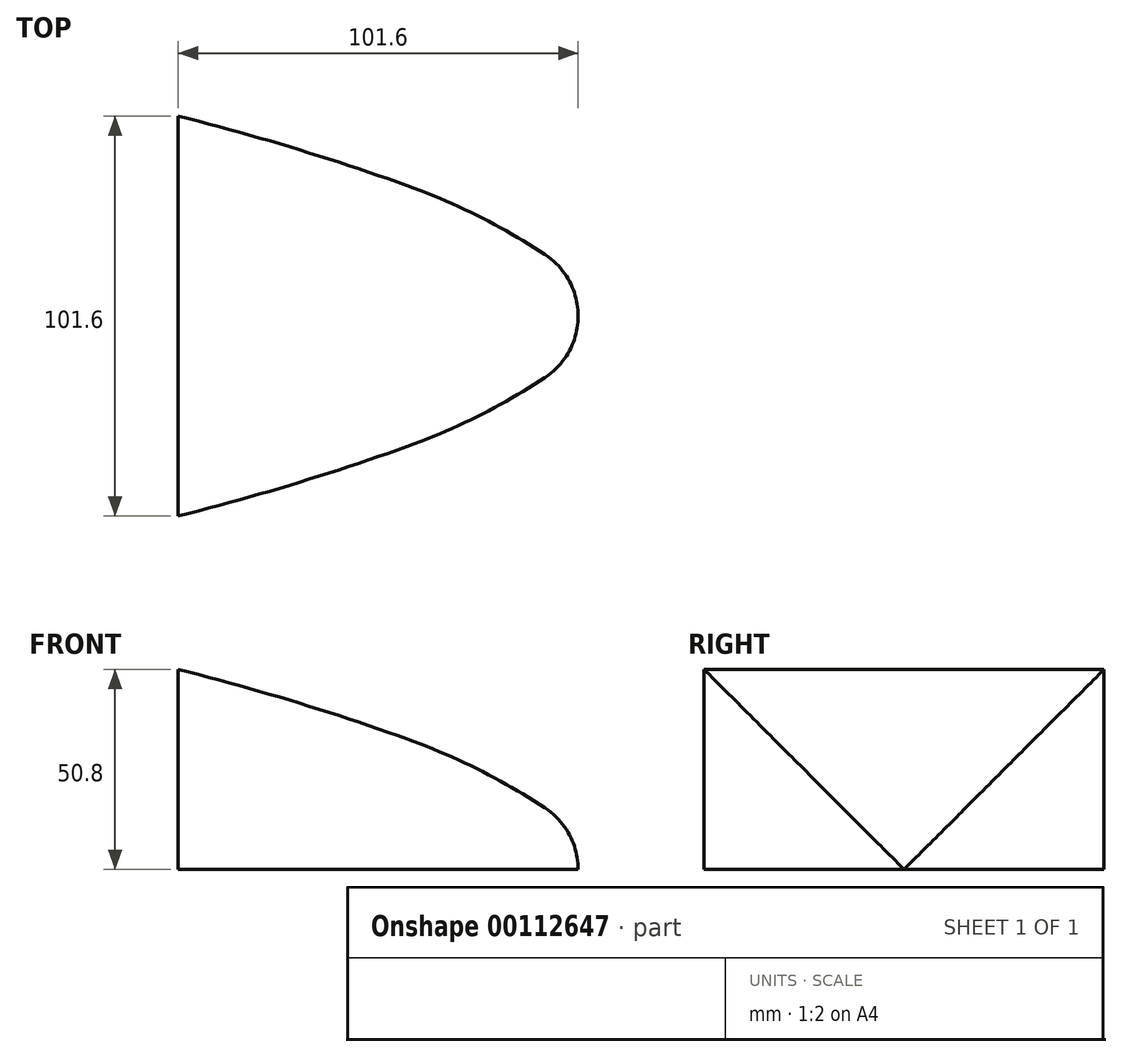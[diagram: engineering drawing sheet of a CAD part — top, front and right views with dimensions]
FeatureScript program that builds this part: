
annotation { "Feature Type Name" : "Feature", "Feature Type Description" : "" }
export const myFeature = defineFeature(function(context is Context, id is Id, definition is map)
    precondition{}
    {
        {
            var Q0;
            Q0=qCreatedBy(makeId("Top.planeOp"),FACE);
            var sketch = newSketch(context, id + "F0", { "sketchPlane" : qUnion([Q0])});
            skLineSegment(sketch, "E0", {"start": v(0, 0) * mm, "end": v(-25.4, 0) * mm, "construction": true});
            skLineSegment(sketch, "E1", {"start": v(0, 0) * mm, "end": v(0, -25.4) * mm, "construction": true});
            skLineSegment(sketch, "E2", {"start": v(0, -25.4) * mm, "end": v(-25.4, -25.4) * mm, "construction": true});
            skLineSegment(sketch, "E3", {"start": v(-25.4, 0) * mm, "end": v(-25.4, -25.4) * mm, "construction": true});
            skArc(sketch, "E4", {"start": v(-8.41, -15.61) * mm, "mid": v(-2.24, -8.87) * mm, "end": v(0, 0) * mm});
            skLineSegment(sketch, "E5", {"start": v(0, 0) * mm, "end": v(-25.4, -25.4) * mm, "construction": true});
            skLineSegment(sketch, "E6", {"start": v(-25.4, -25.4) * mm, "end": v(-50.8, -25.4) * mm, "construction": true});
            skLineSegment(sketch, "E7", {"start": v(-50.8, -25.4) * mm, "end": v(-76.2, -25.4) * mm, "construction": true});
            skLineSegment(sketch, "E8", {"start": v(-76.2, -25.4) * mm, "end": v(-76.2, -50.8) * mm, "construction": true});
            skLineSegment(sketch, "E9", {"start": v(-25.4, -25.4) * mm, "end": v(-76.2, -50.8) * mm, "construction": true});
            skLineSegment(sketch, "E10", {"start": v(0, -25.4) * mm, "end": v(0, -50.8) * mm, "construction": true});
            skLineSegment(sketch, "E11", {"start": v(0, -50.8) * mm, "end": v(-25.4, -50.8) * mm, "construction": true});
            skLineSegment(sketch, "E12", {"start": v(-25.4, -25.4) * mm, "end": v(-25.4, -50.8) * mm, "construction": true});
            skLineSegment(sketch, "E13", {"start": v(-76.2, -25.4) * mm, "end": v(-101.6, -25.4) * mm, "construction": true});
            skLineSegment(sketch, "E14", {"start": v(-101.6, -25.4) * mm, "end": v(-101.6, -50.8) * mm, "construction": true});
            skLineSegment(sketch, "E15", {"start": v(-76.2, -50.8) * mm, "end": v(-50.8, -50.8) * mm, "construction": true});
            skLineSegment(sketch, "E16", {"start": v(-50.8, -50.8) * mm, "end": v(-25.4, -50.8) * mm, "construction": true});
            skLineSegment(sketch, "E17", {"start": v(-76.2, -50.8) * mm, "end": v(-101.6, -50.8) * mm, "construction": true});
            skLineSegment(sketch, "E18", {"start": v(-101.6, -50.8) * mm, "end": v(-127, -50.8) * mm, "construction": true});
            skLineSegment(sketch, "E19", {"start": v(-127, -50.8) * mm, "end": v(-152.4, -50.8) * mm, "construction": true});
            skLineSegment(sketch, "E20", {"start": v(-152.4, -50.8) * mm, "end": v(-177.8, -50.8) * mm, "construction": true});
            skLineSegment(sketch, "E21", {"start": v(-177.8, -50.8) * mm, "end": v(-203.2, -50.8) * mm, "construction": true});
            skLineSegment(sketch, "E22", {"start": v(-203.2, -50.8) * mm, "end": v(-203.2, -76.2) * mm, "construction": true});
            skLineSegment(sketch, "E23", {"start": v(-101.6, -50.8) * mm, "end": v(-203.2, -76.2) * mm, "construction": true});
            skArc(sketch, "E24", {"start": v(-101.6, -50.8) * mm, "mid": v(-72.29, -42.69) * mm, "end": v(-43.42, -33.11) * mm});
            skArc(sketch, "E25", {"start": v(-43.42, -33.11) * mm, "mid": v(-25.4, -25.4) * mm, "end": v(-8.41, -15.61) * mm});
            skLineSegment(sketch, "E26", {"start": v(0, 0) * mm, "end": v(-101.6, 0) * mm});
            skLineSegment(sketch, "E27", {"start": v(-101.6, -50.8) * mm, "end": v(-101.6, 0) * mm});
            skArc(sketch, "E28", {"start": v(0, 0) * mm, "mid": v(-2.24, 8.87) * mm, "end": v(-8.41, 15.61) * mm});
            skArc(sketch, "E29", {"start": v(-8.41, 15.61) * mm, "mid": v(-25.4, 25.4) * mm, "end": v(-43.42, 33.11) * mm});
            skLineSegment(sketch, "E30", {"start": v(-25.4, 0) * mm, "end": v(-25.4, 25.4) * mm, "construction": true});
            skArc(sketch, "E31", {"start": v(-43.42, 33.11) * mm, "mid": v(-72.29, 42.69) * mm, "end": v(-101.6, 50.8) * mm});
            skLineSegment(sketch, "E32", {"start": v(-101.6, 0) * mm, "end": v(-101.6, 50.8) * mm});
            skSolve(sketch);
        }
        {
            var Q0;
            Q0=makeQuery(id+"F0.imprint","IMPRINT",FACE,{"disambiguationData":[TD([[makeQuery(id+"F0.imprint","IMPRINT",EDGE,{"derivedFrom":sQuery(id+"F0.wireOp",EDGE,"E4")}),1.0]])]});
            var Q1;
            Q1=makeQuery(id+"F0.imprint","IMPRINT",FACE,{"disambiguationData":[TD([[makeQuery(id+"F0.imprint","IMPRINT",EDGE,{"derivedFrom":sQuery(id+"F0.wireOp",EDGE,"E26")}),-1.0]])]});
            extrude(context, id + "F1", {"entities" : qUnion([Q0, Q1]), "depth" : 101.6 * mm});
        }
        {
            var Q0;
            Q0=qCreatedBy(makeId("Front.planeOp"),FACE);
            var sketch = newSketch(context, id + "F2", { "sketchPlane" : qUnion([Q0])});
            skArc(sketch, "E33", {"start": v(0, 0) * mm, "mid": v(-2.24, 8.87) * mm, "end": v(-8.41, 15.61) * mm});
            skLineSegment(sketch, "E34.bottom", {"start": v(0, 0) * mm, "end": v(-101.6, 0) * mm, "construction": true});
            skLineSegment(sketch, "E34.top", {"start": v(0, 464.33) * mm, "end": v(-101.6, 464.33) * mm});
            skLineSegment(sketch, "E34.left", {"start": v(0, 0) * mm, "end": v(0, 464.33) * mm});
            skLineSegment(sketch, "E34.right", {"start": v(-101.6, 0) * mm, "end": v(-101.6, 464.33) * mm});
            skArc(sketch, "E35", {"start": v(-8.41, 15.61) * mm, "mid": v(-25.4, 25.4) * mm, "end": v(-43.42, 33.11) * mm});
            skArc(sketch, "E36", {"start": v(-43.42, 33.11) * mm, "mid": v(-72.29, 42.69) * mm, "end": v(-101.6, 50.8) * mm});
            skLineSegment(sketch, "E37", {"start": v(-101.6, 50.8) * mm, "end": v(-203.2, 50.8) * mm, "construction": true});
            skLineSegment(sketch, "E38", {"start": v(-203.2, 50.8) * mm, "end": v(-203.2, 76.2) * mm, "construction": true});
            skLineSegment(sketch, "E39", {"start": v(-203.2, 76.2) * mm, "end": v(-101.6, 50.8) * mm, "construction": true});
            skSolve(sketch);
        }
        {
            var Q0;
            Q0 = qSketchRegion(id + "F2", true);
            var Q1;
            Q1=makeQuery(id+"F1.opExtrude","SWEPT_FACE",FACE,{"disambiguationData":[OSD([sQuery(id+"F0.wireOp",EDGE,"E24")])]});
            var Q2;
            Q2=makeQuery(id+"F1.opExtrude","SWEPT_FACE",FACE,{"disambiguationData":[OSD([sQuery(id+"F0.wireOp",EDGE,"E24")])]});
            extrude(context, id + "F3", {"entities" : qUnion([Q0]), "operationType" : NewBodyOperationType.REMOVE, "endBound" : BoundingType.UP_TO_SURFACE, "oppositeDirection" : true, "endBoundEntityFace" : qUnion([Q1]), "depth" : 25.4 * mm, "hasSecondDirection" : true, "secondDirectionBound" : SecondDirectionBoundingType.UP_TO_SURFACE, "secondDirectionOppositeDirection" : false, "secondDirectionBoundEntityFace" : qUnion([Q2]), "secondDirectionDepth" : 25.4 * mm});
        }
    });
